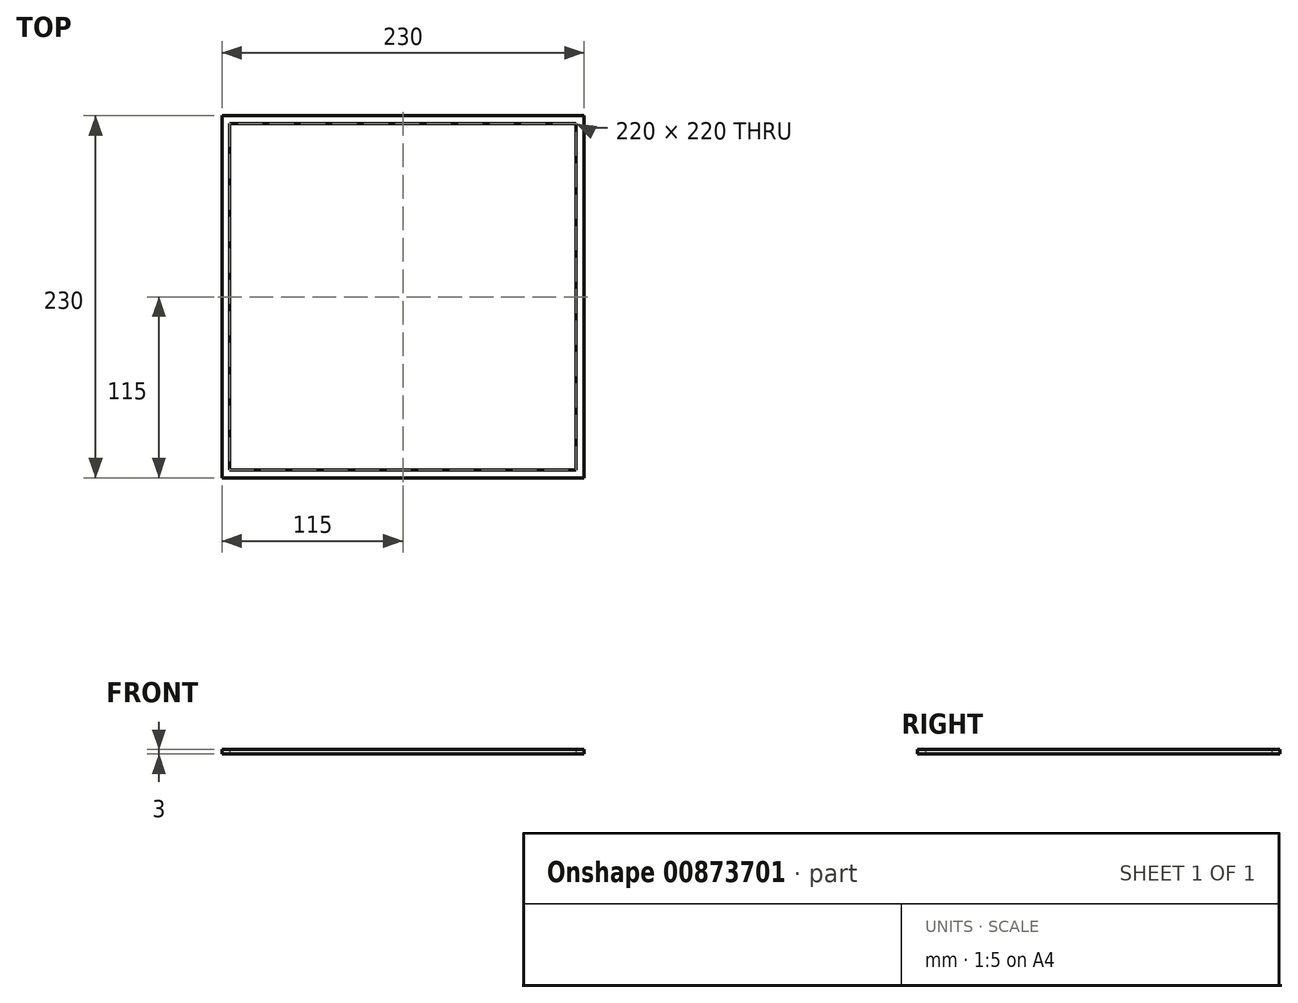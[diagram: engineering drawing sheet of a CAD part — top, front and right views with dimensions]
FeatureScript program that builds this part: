
annotation { "Feature Type Name" : "Feature", "Feature Type Description" : "" }
export const myFeature = defineFeature(function(context is Context, id is Id, definition is map)
    precondition{}
    {
        {
            var Q0;
            Q0=qCreatedBy(makeId("Top.planeOp"),FACE);
            var sketch = newSketch(context, id + "F0", { "sketchPlane" : qUnion([Q0])});
            skLineSegment(sketch, "E0.bottom", {"start": v(-115, 115) * mm, "end": v(115, 115) * mm});
            skLineSegment(sketch, "E0.top", {"start": v(-115, -115) * mm, "end": v(115, -115) * mm});
            skLineSegment(sketch, "E0.left", {"start": v(-115, 115) * mm, "end": v(-115, -115) * mm});
            skLineSegment(sketch, "E0.right", {"start": v(115, 115) * mm, "end": v(115, -115) * mm});
            skLineSegment(sketch, "E1.0", {"start": v(-110, 110) * mm, "end": v(110, 110) * mm});
            skLineSegment(sketch, "E1.1", {"start": v(-110, 110) * mm, "end": v(-110, -110) * mm});
            skLineSegment(sketch, "E1.2", {"start": v(-110, -110) * mm, "end": v(110, -110) * mm});
            skLineSegment(sketch, "E1.3", {"start": v(110, 110) * mm, "end": v(110, -110) * mm});
            skSolve(sketch);
        }
        {
            var Q0;
            Q0=makeQuery(id+"F0.imprint","IMPRINT",FACE,{"disambiguationData":[TD([[makeQuery(id+"F0.imprint","IMPRINT",EDGE,{"derivedFrom":sQuery(id+"F0.wireOp",EDGE,"E0.bottom")}),-1.0]])]});
            extrude(context, id + "F1", {"entities" : qUnion([Q0]), "depth" : 3 * mm, "offsetDistance" : 25 * mm});
        }
    });
